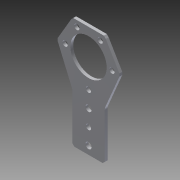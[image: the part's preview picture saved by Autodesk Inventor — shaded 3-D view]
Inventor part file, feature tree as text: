
AUTODESK INVENTOR PART (.ipt)
format: ipt  version: 2014 (Build 180170000, 170)  size: 167,424 bytes
history: native  units: in
note: dims shown in document units (in); Inventor stores cm internally (conversion verified against a paired STEP export)
features: other x2, extrude x1, imported_body x1, sketch x1
ambient origin geometry x8: Origin, YZ Plane, XZ Plane, XY Plane, X Axis, Y Axis, Z Axis, Center Point
bodies: Body1 (feature_tree)
feature tree (5):
  other  "Cut-Extrude1"
  other  "217-3554-STEP1"
  extrude  "Extrusion1"  Depth=1.0in TaperAngle=0.0deg
  imported_body  "Base1"
  sketch  "Sketch2"  dims[d1=0.19in d2=1.0in d3=0.0in]
